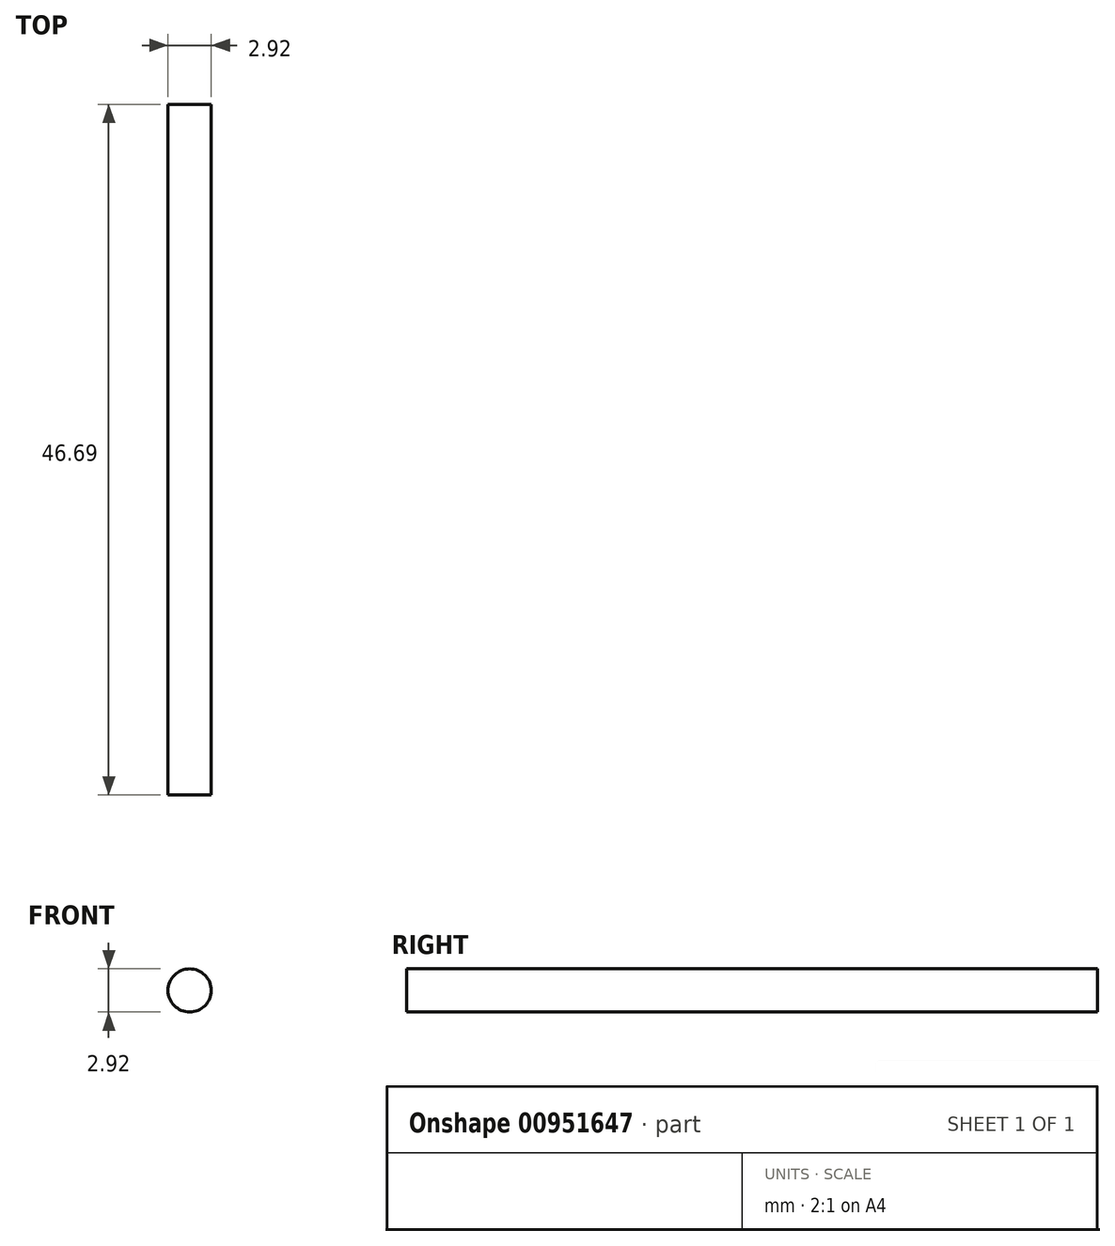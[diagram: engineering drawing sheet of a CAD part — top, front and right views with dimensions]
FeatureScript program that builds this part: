
annotation { "Feature Type Name" : "Feature", "Feature Type Description" : "" }
export const myFeature = defineFeature(function(context is Context, id is Id, definition is map)
    precondition{}
    {
        {
            var Q0;
            Q0=qCreatedBy(makeId("Front.planeOp"),FACE);
            var sketch = newSketch(context, id + "F0", { "sketchPlane" : qUnion([Q0])});
            skCircle(sketch, "E0", {"center": v(0, 0) * mm, "radius": 1.46 * mm});
            skSolve(sketch);
        }
        {
            var Q0;
            Q0 = qSketchRegion(id + "F0", true);
            extrude(context, id + "F1", {"entities" : qUnion([Q0]), "depth" : 46.69 * mm, "offsetDistance" : 25 * mm});
        }
    });
